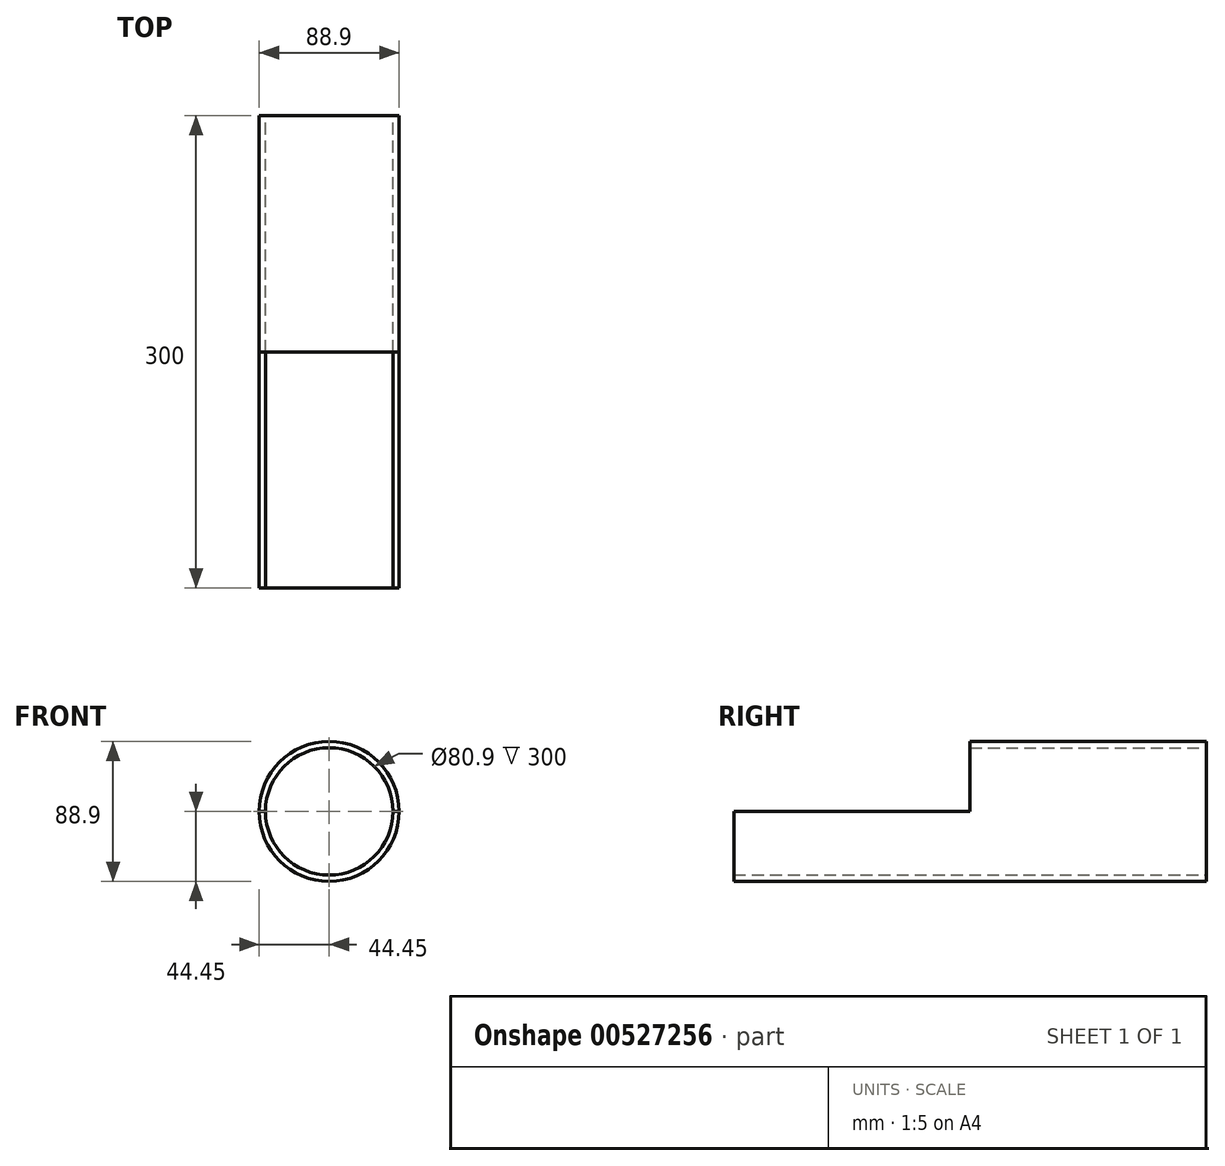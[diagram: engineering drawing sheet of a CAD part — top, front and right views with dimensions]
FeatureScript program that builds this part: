
annotation { "Feature Type Name" : "Feature", "Feature Type Description" : "" }
export const myFeature = defineFeature(function(context is Context, id is Id, definition is map)
    precondition{}
    {
        {
            var Q0;
            Q0=qCreatedBy(makeId("Front.planeOp"),FACE);
            var sketch = newSketch(context, id + "F0", { "sketchPlane" : qUnion([Q0])});
            skCircle(sketch, "E0", {"center": v(0, 0) * mm, "radius": 44.45 * mm});
            skSolve(sketch);
        }
        {
            var Q0;
            Q0=makeQuery(id+"F0.imprint","IMPRINT",FACE,{"disambiguationData":[TD([[makeQuery(id+"F0.imprint","IMPRINT",EDGE,{"derivedFrom":sQuery(id+"F0.wireOp",EDGE,"E0")}),1.0]])]});
            extrude(context, id + "F1", {"entities" : qUnion([Q0]), "depth" : 300 * mm, "offsetDistance" : 25 * mm});
        }
        {
            var Q0;
            Q0=makeQuery(id+"F1.opExtrude","CAP_FACE",FACE,{"disambiguationData":[OSD([sQuery(id+"F0.wireOp",EDGE,"E0")])],"isStart":false});
            var sketch = newSketch(context, id + "F2", { "sketchPlane" : qUnion([Q0])});
            skLineSegment(sketch, "E1", {"start": v(-44.45, 0) * mm, "end": v(44.45, 0) * mm});
            skArc(sketch, "E2", {"start": v(-44.45, 0) * mm, "mid": v(0, 44.45) * mm, "end": v(44.45, 0) * mm});
            skSolve(sketch);
        }
        {
            var Q0;
            Q0=makeQuery(id+"F2.imprint","IMPRINT",FACE,{"disambiguationData":[TD([[makeQuery(id+"F2.imprint","IMPRINT",EDGE,{"derivedFrom":sQuery(id+"F2.wireOp",EDGE,"E1")}),1.0]])]});
            extrude(context, id + "F3", {"entities" : qUnion([Q0]), "operationType" : NewBodyOperationType.REMOVE, "oppositeDirection" : true, "depth" : 150 * mm, "offsetDistance" : 25 * mm});
        }
        {
            var Q0;
            Q0=makeQuery(id+"F1.opExtrude","CAP_FACE",FACE,{"disambiguationData":[OSD([sQuery(id+"F0.wireOp",EDGE,"E0")])],"isStart":true});
            var sketch = newSketch(context, id + "F4", { "sketchPlane" : qUnion([Q0])});
            skCircle(sketch, "E3", {"center": v(0, 0) * mm, "radius": 40.45 * mm});
            skSolve(sketch);
        }
        {
            var Q0;
            Q0=sQuery(id+"F4.wireOp",VERTEX,"E3.center");
            var Q1;
            Q1=makeQuery(id+"F1.opExtrude","SWEPT_BODY",BODY,{"disambiguationData":[OSD([sQuery(id+"F0.wireOp",EDGE,"E0")])]});
            hole(context, id + "F5", {"style" : HoleStyle.SIMPLE, "endStyle" : HoleEndStyle.BLIND, "holeDiameter" : 80.9 * mm, "majorDiameter" : 5 * mm, "holeDepth" : 300 * mm, "isTappedThrough" : true, "tappedDepth" : 12 * mm, "tapClearance" : 3, "startFromSketch" : true, "locations" : qUnion([Q0]), "scope" : qUnion([Q1])});
        }
    });
